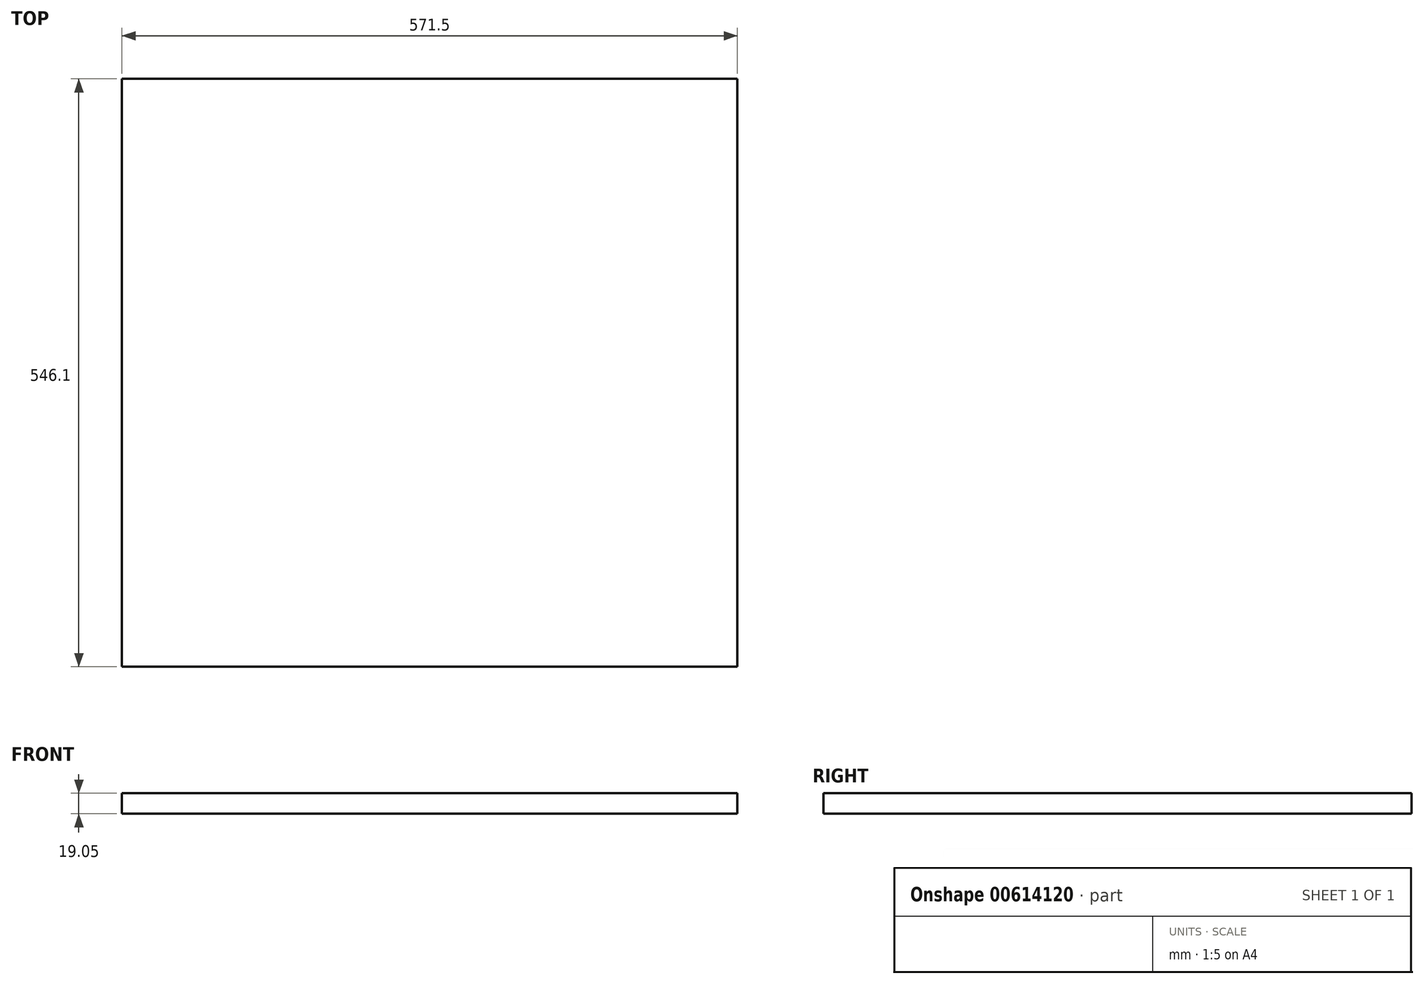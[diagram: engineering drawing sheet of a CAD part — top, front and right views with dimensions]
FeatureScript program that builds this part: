
annotation { "Feature Type Name" : "Feature", "Feature Type Description" : "" }
export const myFeature = defineFeature(function(context is Context, id is Id, definition is map)
    precondition{}
    {
        {
            var Q0;
            Q0=qCreatedBy(makeId("Top.planeOp"),FACE);
            var sketch = newSketch(context, id + "F0", { "sketchPlane" : qUnion([Q0])});
            skLineSegment(sketch, "E0.bottom", {"start": v(285.75, 273.05) * mm, "end": v(-285.75, 273.05) * mm});
            skLineSegment(sketch, "E0.top", {"start": v(285.75, -273.05) * mm, "end": v(-285.75, -273.05) * mm});
            skLineSegment(sketch, "E0.left", {"start": v(285.75, 273.05) * mm, "end": v(285.75, -273.05) * mm});
            skLineSegment(sketch, "E0.right", {"start": v(-285.75, 273.05) * mm, "end": v(-285.75, -273.05) * mm});
            skPoint(sketch, "E0.middle", {"position": v(0, 0) * mm});
            skSolve(sketch);
        }
        {
            var Q0;
            Q0=makeQuery(id+"F0.imprint","IMPRINT",FACE,{"disambiguationData":[TD([[makeQuery(id+"F0.imprint","IMPRINT",EDGE,{"derivedFrom":sQuery(id+"F0.wireOp",EDGE,"E0.bottom")}),1.0]])]});
            extrude(context, id + "F1", {"entities" : qUnion([Q0]), "depth" : 19.05 * mm, "offsetDistance" : 25.4 * mm});
        }
    });
